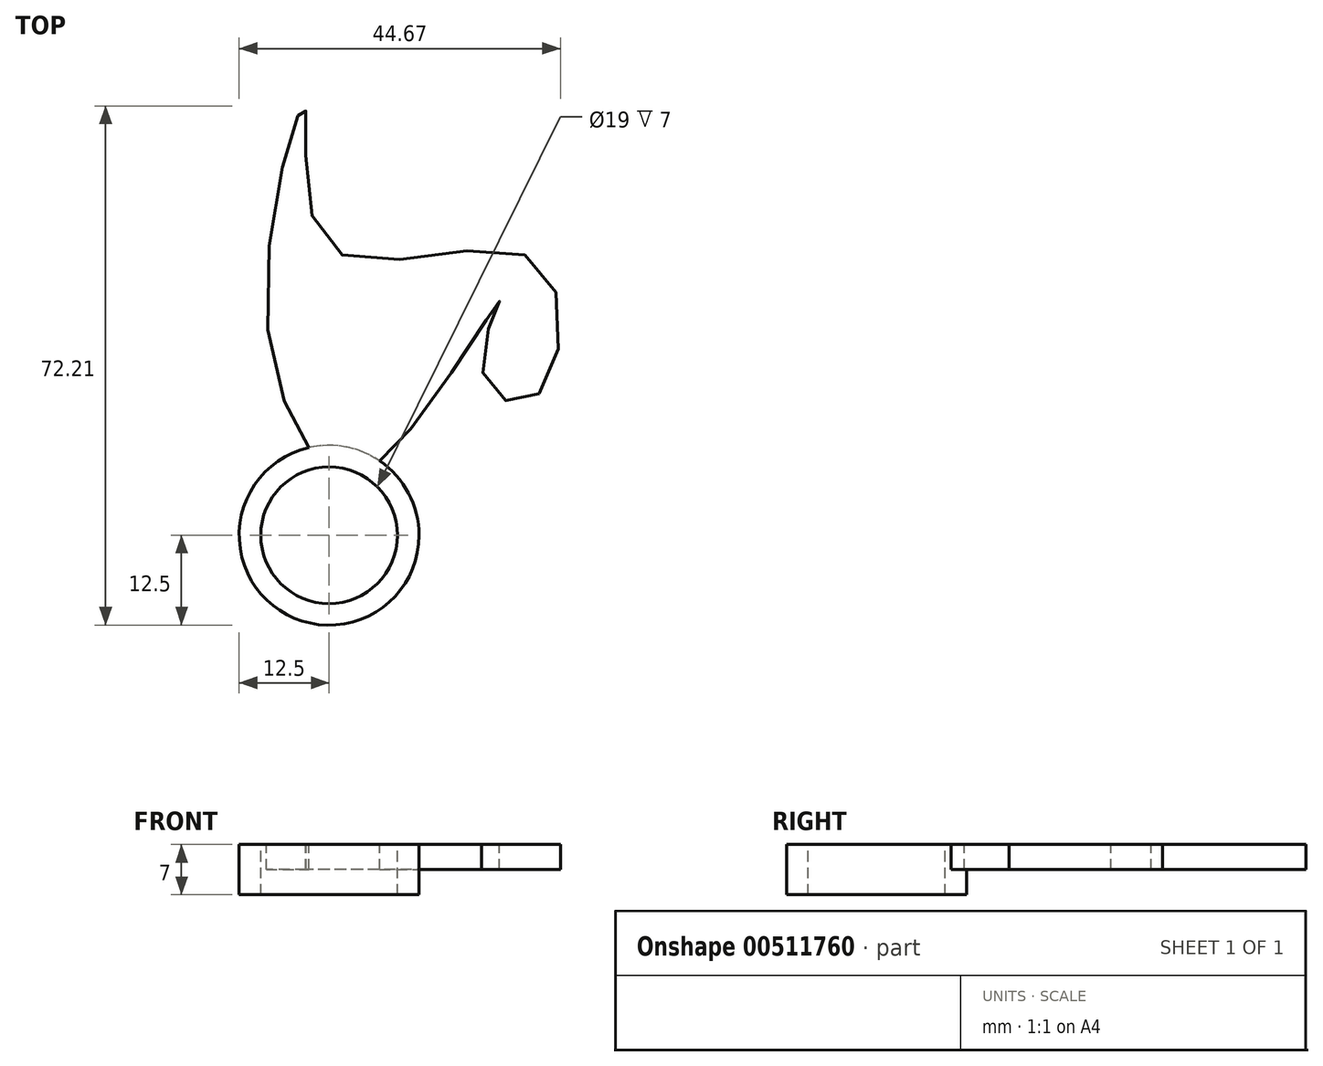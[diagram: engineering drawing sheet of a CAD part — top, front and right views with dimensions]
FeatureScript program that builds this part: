
annotation { "Feature Type Name" : "Feature", "Feature Type Description" : "" }
export const myFeature = defineFeature(function(context is Context, id is Id, definition is map)
    precondition{}
    {
        {
            var Q0;
            Q0=qCreatedBy(makeId("Top.planeOp"),FACE);
            var sketch = newSketch(context, id + "F0", { "sketchPlane" : qUnion([Q0])});
            skCircle(sketch, "E0", {"center": v(0, 0) * mm, "radius": 12.5 * mm});
            skSolve(sketch);
        }
        {
            var Q0;
            Q0=makeQuery(id+"F0.imprint","IMPRINT",FACE,{"disambiguationData":[TD([[makeQuery(id+"F0.imprint","IMPRINT",EDGE,{"derivedFrom":sQuery(id+"F0.wireOp",EDGE,"E0")}),1.0]])]});
            extrude(context, id + "F1", {"entities" : qUnion([Q0]), "oppositeDirection" : true, "depth" : 7 * mm});
        }
        {
            var Q0;
            Q0=qCreatedBy(makeId("Top.planeOp"),FACE);
            var sketch = newSketch(context, id + "F2", { "sketchPlane" : qUnion([Q0])});
            skCircle(sketch, "E1", {"center": v(0, 0) * mm, "radius": 9.5 * mm});
            skSolve(sketch);
        }
        {
            var Q0;
            Q0=makeQuery(id+"F2.imprint","IMPRINT",FACE,{"disambiguationData":[TD([[makeQuery(id+"F2.imprint","IMPRINT",EDGE,{"derivedFrom":sQuery(id+"F2.wireOp",EDGE,"E1")}),1.0]])]});
            extrude(context, id + "F3", {"entities" : qUnion([Q0]), "operationType" : NewBodyOperationType.REMOVE, "endBound" : BoundingType.THROUGH_ALL, "oppositeDirection" : true, "depth" : 7 * mm});
        }
        {
            var Q0;
            Q0=qCreatedBy(makeId("Top.planeOp"),FACE);
            var sketch = newSketch(context, id + "F4", { "sketchPlane" : qUnion([Q0])});
            skFitSpline(sketch, "E2", {"points": [v(9.1, 12.13) * mm, v(23.69, 32.59) * mm, v(21.34, 22.71) * mm, v(28.62, 19.18) * mm, v(28.62, 38.23) * mm, v(0, 40.11) * mm, v(-3.35, 59.63) * mm, v(-8.53, 28.59) * mm, v(0, 10.34) * mm, v(1.44, 11.98) * mm, v(4.17, 10.25) * mm, v(9.1, 12.13) * mm]});
            skSolve(sketch);
        }
        {
            var Q0;
            Q0=makeQuery(id+"F4.imprint","IMPRINT",FACE,{"disambiguationData":[TD([[makeQuery(id+"F4.imprint","IMPRINT",EDGE,{"derivedFrom":sQuery(id+"F4.wireOp",EDGE,"E2")}),1.0]])]});
            var Q1;
            Q1=sQuery(id+"F4.wireOp",EDGE,"E2");
            extrude(context, id + "F5", {"entities" : qUnion([Q0]), "operationType" : NewBodyOperationType.ADD, "surfaceEntities" : qUnion([Q1]), "oppositeDirection" : true, "depth" : (7 / 2) * mm});
        }
    });
